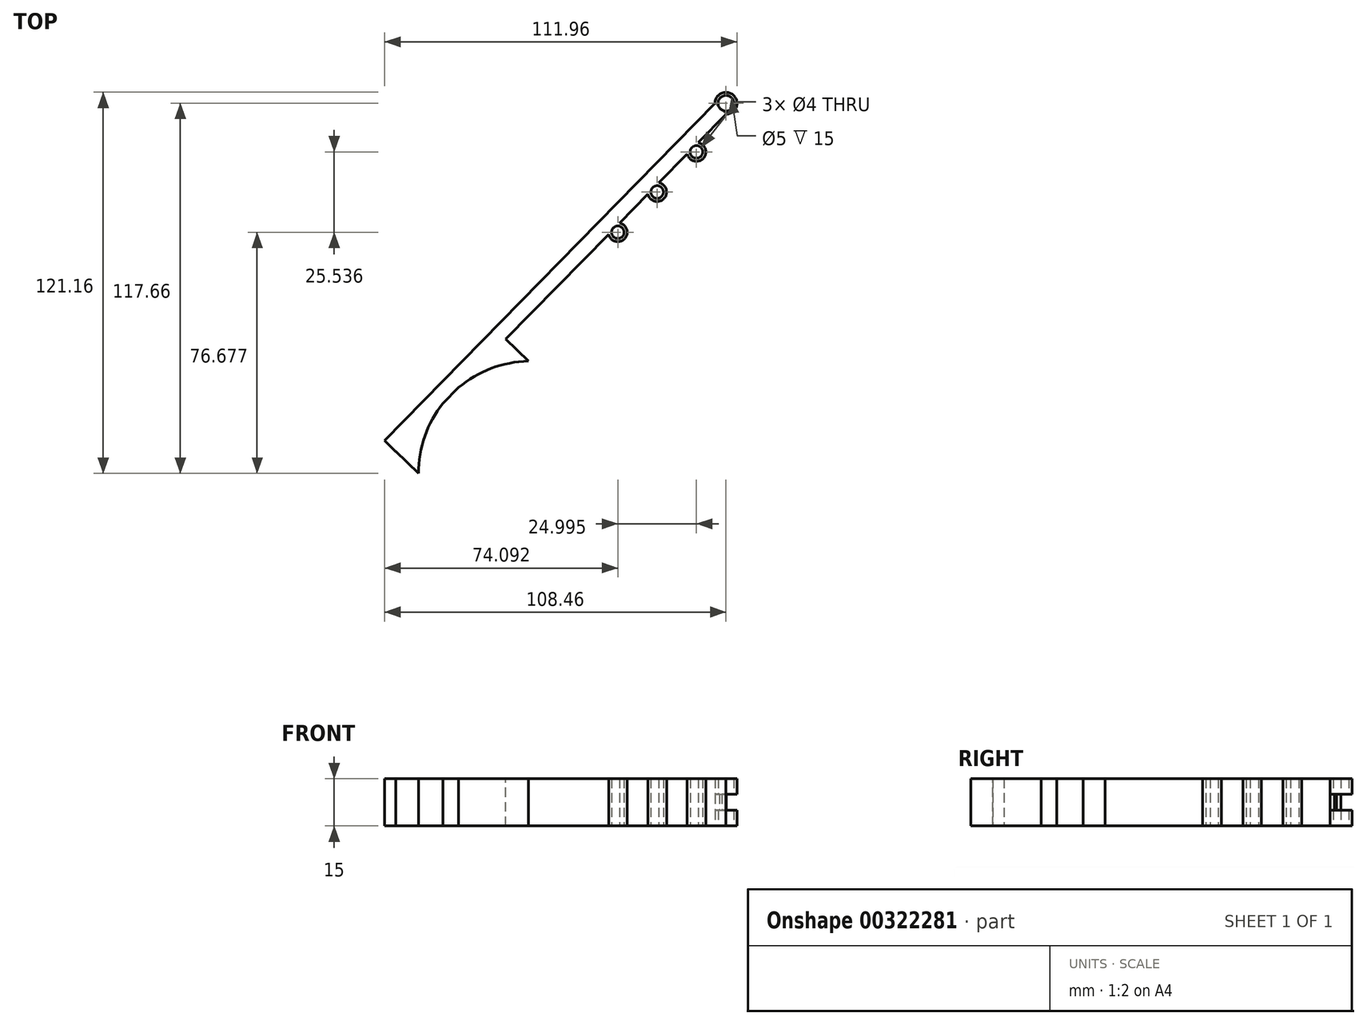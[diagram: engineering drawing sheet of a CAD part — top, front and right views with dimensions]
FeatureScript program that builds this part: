
annotation { "Feature Type Name" : "Feature", "Feature Type Description" : "" }
export const myFeature = defineFeature(function(context is Context, id is Id, definition is map)
    precondition{}
    {
        {
            var Q0;
            Q0=qCreatedBy(makeId("Top.planeOp"),FACE);
            var sketch = newSketch(context, id + "F0", { "sketchPlane" : qUnion([Q0])});
            skCircle(sketch, "E0", {"center": v(0, 0) * mm, "radius": 3.5 * mm});
            skPoint(sketch, "E1", {"position": v(0, -3.5) * mm});
            skPoint(sketch, "E2", {"position": v(-3.5, 0) * mm});
            skLineSegment(sketch, "E3", {"start": v(0, -3.5) * mm, "end": v(-104.92, -110.7) * mm});
            skLineSegment(sketch, "E4", {"start": v(-3.5, 0) * mm, "end": v(-108.46, -107.16) * mm});
            skLineSegment(sketch, "E5", {"start": v(-104.92, -110.7) * mm, "end": v(-108.46, -107.16) * mm});
            skPoint(sketch, "E6", {"position": v(-34.97, -39.23) * mm});
            skPoint(sketch, "E7", {"position": v(-8.8, -12.5) * mm});
            skPoint(sketch, "E8", {"position": v(-12.3, -16.07) * mm});
            skPoint(sketch, "E9", {"position": v(-21.3, -25.27) * mm});
            skPoint(sketch, "E10", {"position": v(-24.8, -28.84) * mm});
            skPoint(sketch, "E11", {"position": v(-33.8, -38.04) * mm});
            skPoint(sketch, "E12", {"position": v(-37.3, -41.6) * mm});
            skArc(sketch, "E13", {"start": v(-24.8, -28.84) * mm, "mid": v(-19.73, -30.31) * mm, "end": v(-21.3, -25.27) * mm});
            skArc(sketch, "E14", {"start": v(-12.3, -16.07) * mm, "mid": v(-7.23, -17.55) * mm, "end": v(-8.8, -12.5) * mm});
            skArc(sketch, "E15", {"start": v(-37.3, -41.6) * mm, "mid": v(-32.22, -43.08) * mm, "end": v(-33.8, -38.04) * mm});
            skSolve(sketch);
        }
        {
            var Q0;
            Q0=makeQuery(id+"F0.imprint","IMPRINT",FACE,{"disambiguationData":[TD([[makeQuery(id+"F0.imprint","IMPRINT",EDGE,{"derivedFrom":sQuery(id+"F0.wireOp",EDGE,"E0")}),1.0]])]});
            extrude(context, id + "F1", {"entities" : qUnion([Q0]), "depth" : 15 * mm});
        }
        {
            var Q0;
            Q0 = qSketchRegion(id + "F0", true);
            extrude(context, id + "F2", {"entities" : qUnion([Q0]), "operationType" : NewBodyOperationType.ADD, "depth" : 15 * mm});
        }
        {
            var Q0;
            Q0=makeQuery(id+"F2.opExtrude","SWEPT_FACE",FACE,{"disambiguationData":[OSD([sQuery(id+"F0.wireOp",EDGE,"E4")])]});
            var sketch = newSketch(context, id + "F3", { "sketchPlane" : qUnion([Q0])});
            skLineSegment(sketch, "E16.bottom", {"start": v(2.45, 10.03) * mm, "end": v(9.9, 10.03) * mm});
            skLineSegment(sketch, "E16.top", {"start": v(2.45, 4.97) * mm, "end": v(9.9, 4.97) * mm});
            skLineSegment(sketch, "E16.left", {"start": v(2.45, 10.03) * mm, "end": v(2.45, 4.97) * mm});
            skLineSegment(sketch, "E16.right", {"start": v(9.9, 10.03) * mm, "end": v(9.9, 4.97) * mm});
            skSolve(sketch);
        }
        {
            var Q0;
            Q0=makeQuery(id+"F3.imprint","IMPRINT",FACE,{"disambiguationData":[TD([[makeQuery(id+"F3.imprint","IMPRINT",EDGE,{"derivedFrom":sQuery(id+"F3.wireOp",EDGE,"E16.bottom")}),-1.0]])]});
            extrude(context, id + "F4", {"entities" : qUnion([Q0]), "operationType" : NewBodyOperationType.ADD, "depth" : 25 * mm});
        }
        {
            var Q0;
            Q0=makeQuery(id+"F4.opExtrude","SWEPT_FACE",FACE,{"disambiguationData":[OSD([sQuery(id+"F3.wireOp",EDGE,"E16.left")])]});
            var sketch = newSketch(context, id + "F5", { "sketchPlane" : qUnion([Q0])});
            skLineSegment(sketch, "E17.bottom", {"start": v(2.5, 10.03) * mm, "end": v(11.38, 10.03) * mm});
            skLineSegment(sketch, "E17.top", {"start": v(2.5, 4.97) * mm, "end": v(11.38, 4.97) * mm});
            skLineSegment(sketch, "E17.left", {"start": v(2.5, 10.03) * mm, "end": v(2.5, 4.97) * mm});
            skLineSegment(sketch, "E17.right", {"start": v(11.38, 10.03) * mm, "end": v(11.38, 4.97) * mm});
            skSolve(sketch);
        }
        {
            var Q0;
            Q0=makeQuery(id+"F5.imprint","IMPRINT",FACE,{"disambiguationData":[TD([[makeQuery(id+"F5.imprint","IMPRINT",EDGE,{"derivedFrom":sQuery(id+"F5.wireOp",EDGE,"E17.bottom")}),1.0]])]});
            extrude(context, id + "F6", {"entities" : qUnion([Q0]), "operationType" : NewBodyOperationType.REMOVE, "depth" : 25 * mm});
        }
        {
            var Q0;
            Q0=makeQuery(id+"F6.boolean.opBoolean","COPY",FACE,{"derivedFrom":makeQuery(id+"F6.opExtrude","SWEPT_FACE",FACE,{"disambiguationData":[OSD([sQuery(id+"F5.wireOp",EDGE,"E17.left")])]})});
            var sketch = newSketch(context, id + "F7", { "sketchPlane" : qUnion([Q0])});
            skLineSegment(sketch, "E18.bottom", {"start": v(2.45, 10.03) * mm, "end": v(-2.45, 10.03) * mm});
            skLineSegment(sketch, "E18.top", {"start": v(2.45, 4.97) * mm, "end": v(-2.45, 4.97) * mm});
            skLineSegment(sketch, "E18.left", {"start": v(2.45, 10.03) * mm, "end": v(2.45, 4.97) * mm});
            skLineSegment(sketch, "E18.right", {"start": v(-2.45, 10.03) * mm, "end": v(-2.45, 4.97) * mm});
            skSolve(sketch);
        }
        {
            var Q0;
            Q0=makeQuery(id+"F7.imprint","IMPRINT",FACE,{"disambiguationData":[TD([[makeQuery(id+"F7.imprint","IMPRINT",EDGE,{"derivedFrom":sQuery(id+"F7.wireOp",EDGE,"E18.bottom")}),-1.0]])]});
            extrude(context, id + "F8", {"entities" : qUnion([Q0]), "operationType" : NewBodyOperationType.REMOVE, "oppositeDirection" : true, "depth" : 25 * mm});
        }
        {
            var Q0;
            Q0=makeQuery(id+"F8.boolean.opBoolean","COPY",FACE,{"derivedFrom":makeQuery(id+"F8.opExtrude","SWEPT_FACE",FACE,{"disambiguationData":[OSD([sQuery(id+"F7.wireOp",EDGE,"E18.right")])]})});
            extrude(context, id + "F9", {"entities" : qUnion([Q0]), "operationType" : NewBodyOperationType.REMOVE, "oppositeDirection" : true, "depth" : 25 * mm});
        }
        {
            var Q0;
            Q0=makeQuery(id+"F4.opExtrude","CAP_FACE",FACE,{"disambiguationData":[OSD([sQuery(id+"F3.wireOp",EDGE,"E16.bottom"),sQuery(id+"F3.wireOp",EDGE,"E16.top"),sQuery(id+"F3.wireOp",EDGE,"E16.left"),sQuery(id+"F3.wireOp",EDGE,"E16.right")])],"isStart":false});
            extrude(context, id + "F10", {"entities" : qUnion([Q0]), "operationType" : NewBodyOperationType.REMOVE, "oppositeDirection" : true, "depth" : 25 * mm});
        }
        {
            var Q0;
            {var subQ0=sQuery(id+"F0.wireOp",EDGE,"E0");Q0=makeQuery(id+"F2.boolean.opBoolean","MERGE",FACE,{"derivedFrom":[makeQuery(id+"F1.opExtrude","CAP_FACE",FACE,{"disambiguationData":[OSD([subQ0])],"isStart":true}),makeQuery(id+"F2.opExtrude","CAP_FACE",FACE,{"disambiguationData":[OSD([subQ0,sQuery(id+"F0.wireOp",EDGE,"E3"),sQuery(id+"F0.wireOp",EDGE,"E4"),sQuery(id+"F0.wireOp",EDGE,"E5")])],"isStart":true})]});}
            var sketch = newSketch(context, id + "F11", { "sketchPlane" : qUnion([Q0])});
            skCircle(sketch, "E19", {"center": v(0, 0) * mm, "radius": 2.5 * mm});
            skCircle(sketch, "E20", {"center": v(-34.37, 40.98) * mm, "radius": 2 * mm});
            skCircle(sketch, "E21", {"center": v(-21.87, 28.21) * mm, "radius": 2 * mm});
            skCircle(sketch, "E22", {"center": v(-9.37, 15.45) * mm, "radius": 2 * mm});
            skSolve(sketch);
        }
        {
            var Q0;
            Q0=makeQuery(id+"F11.imprint","IMPRINT",FACE,{"disambiguationData":[TD([[makeQuery(id+"F11.imprint","IMPRINT",EDGE,{"derivedFrom":sQuery(id+"F11.wireOp",EDGE,"E19")}),1.0]])]});
            extrude(context, id + "F12", {"entities" : qUnion([Q0]), "operationType" : NewBodyOperationType.REMOVE, "oppositeDirection" : true, "depth" : 25 * mm});
        }
        {
            var Q0;
            {var subQ0=sQuery(id+"F0.wireOp",EDGE,"E0");Q0=makeQuery(id+"F2.boolean.opBoolean","MERGE",FACE,{"derivedFrom":[makeQuery(id+"F1.opExtrude","CAP_FACE",FACE,{"disambiguationData":[OSD([subQ0])],"isStart":false}),makeQuery(id+"F2.opExtrude","CAP_FACE",FACE,{"disambiguationData":[OSD([subQ0,sQuery(id+"F0.wireOp",EDGE,"E3"),sQuery(id+"F0.wireOp",EDGE,"E4"),sQuery(id+"F0.wireOp",EDGE,"E5")])],"isStart":false})]});}
            var sketch = newSketch(context, id + "F13", { "sketchPlane" : qUnion([Q0])});
            skPoint(sketch, "E23", {"position": v(-97.93, -103.55) * mm});
            skLineSegment(sketch, "E24", {"start": v(-108.46, -107.16) * mm, "end": v(-97.74, -117.66) * mm});
            skPoint(sketch, "E25", {"position": v(-69.95, -74.96) * mm});
            skLineSegment(sketch, "E26", {"start": v(-69.95, -74.96) * mm, "end": v(-73.5, -71.48) * mm});
            skLineSegment(sketch, "E27", {"start": v(-73.5, -71.48) * mm, "end": v(-62.8, -81.97) * mm});
            skArc(sketch, "E28", {"start": v(-62.8, -81.97) * mm, "mid": v(-87.54, -92.69) * mm, "end": v(-97.74, -117.66) * mm});
            skSolve(sketch);
        }
        {
            var Q0;
            {var subQ0=sQuery(id+"F13.wireOp",EDGE,"rqMPopDd-dIjp-rFK5-pnbN-QkaCfsaYLzSV");var subQ1=sQuery(id+"F13.wireOp",EDGE,"E27");var subQ2=makeQuery(id+"F13.imprint","INTERSECT",VERTEX,{"derivedFrom":[subQ1,subQ0]});Q0=makeQuery(id+"F13.imprint","IMPRINT",FACE,{"disambiguationData":[TD([[makeQuery(id+"F13.imprint","IMPRINT",EDGE,{"disambiguationData":[TD([[subQ2,1.0]])],"derivedFrom":subQ1}),-1.0]])]});}
            var Q1;
            {var subQ0=sQuery(id+"F13.wireOp",EDGE,"rqMPopDd-dIjp-rFK5-pnbN-QkaCfsaYLzSV");var subQ1=sQuery(id+"F13.wireOp",EDGE,"E24");var subQ2=makeQuery(id+"F13.imprint","INTERSECT",VERTEX,{"derivedFrom":[subQ1,subQ0]});Q1=makeQuery(id+"F13.imprint","IMPRINT",FACE,{"disambiguationData":[TD([[makeQuery(id+"F13.imprint","IMPRINT",EDGE,{"disambiguationData":[TD([[subQ2,1.0]])],"derivedFrom":subQ1}),1.0]])]});}
            extrude(context, id + "F14", {"entities" : qUnion([Q0, Q1]), "operationType" : NewBodyOperationType.ADD, "oppositeDirection" : true, "depth" : 15 * mm});
        }
        {
            var Q0;
            Q0 = qSketchRegion(id + "F11", true);
            extrude(context, id + "F15", {"entities" : qUnion([Q0]), "operationType" : NewBodyOperationType.REMOVE, "oppositeDirection" : true, "depth" : 25 * mm});
        }
    });
